FCSTD DOCUMENT  (FreeCAD 1.0R39109 (Git))
Label: main
License: All rights reserved
LicenseURL: https://en.wikipedia.org/wiki/All_rights_reserved
objects: Sketcher::SketchObject×1, PartDesign::Body×1
note: 3 computed .brp shape members not serialized (recipe doc carries the construction recipe); baked Part::Feature solids carry a one-line shape summary decoded from their .brp

FEATURE [Sketcher::SketchObject] Sketch
  ArcFitTolerance = 1e-06
  AttachmentSupport = -> [XY_Plane]
  FullyConstrained = true
  MakeInternals = false
  MapMode = 5
  sketch-geometry (28):
    g0: Circle CenterX=-90 CenterY=0 CenterZ=0 NormalX=0 NormalY=0 NormalZ=1 AngleXU=0 Radius=57
    g1: Circle CenterX=0 CenterY=90 CenterZ=0 NormalX=0 NormalY=0 NormalZ=1 AngleXU=0 Radius=57
    g2: Circle CenterX=90 CenterY=0 CenterZ=0 NormalX=0 NormalY=0 NormalZ=1 AngleXU=0 Radius=57
    g3: Circle CenterX=0 CenterY=-90 CenterZ=0 NormalX=0 NormalY=0 NormalZ=1 AngleXU=0 Radius=57
    g4: Circle [constr] CenterX=0 CenterY=0 CenterZ=0 NormalX=0 NormalY=0 NormalZ=1 AngleXU=0 Radius=90
    g5: Circle CenterX=0 CenterY=0 CenterZ=0 NormalX=0 NormalY=0 NormalZ=1 AngleXU=0 Radius=14
    g6: ArcOfCircle CenterX=0 CenterY=90 CenterZ=0 NormalX=0 NormalY=0 NormalZ=1 AngleXU=0 Radius=75 StartAngle=0.0646876 EndAngle=3.07691
    g7: ArcOfCircle CenterX=90 CenterY=0 CenterZ=0 NormalX=0 NormalY=0 NormalZ=1 AngleXU=0 Radius=75 StartAngle=4.77708 EndAngle=7.78929
    g8: ArcOfCircle CenterX=0 CenterY=-90 CenterZ=0 NormalX=0 NormalY=0 NormalZ=1 AngleXU=0 Radius=75 StartAngle=3.20628 EndAngle=6.2185
    g9: ArcOfCircle CenterX=-90 CenterY=0 CenterZ=0 NormalX=0 NormalY=0 NormalZ=1 AngleXU=0 Radius=75 StartAngle=1.63548 EndAngle=4.6477
    g10: ArcOfCircle CenterX=-81.3173 CenterY=81.3173 CenterZ=0 NormalX=0 NormalY=0 NormalZ=1 AngleXU=0 Radius=15 StartAngle=1.12452 EndAngle=3.58787
    g11: LineSegment [constr] StartX=-81.3173 StartY=81.3173 StartZ=0 EndX=0 EndY=0 EndZ=0
    g12: ArcOfCircle CenterX=81.3173 CenterY=81.3173 CenterZ=0 NormalX=0 NormalY=0 NormalZ=1 AngleXU=0 Radius=15 StartAngle=5.83691 EndAngle=8.30026
    g13: ArcOfCircle CenterX=81.3173 CenterY=-81.3173 CenterZ=0 NormalX=0 NormalY=0 NormalZ=1 AngleXU=0 Radius=15 StartAngle=4.26611 EndAngle=6.72946
    g14: ArcOfCircle CenterX=-81.3173 CenterY=-81.3173 CenterZ=0 NormalX=0 NormalY=0 NormalZ=1 AngleXU=0 Radius=15 StartAngle=2.69532 EndAngle=5.15867
    g15: LineSegment [constr] StartX=0 StartY=0 StartZ=0 EndX=81.3173 EndY=81.3173 EndZ=0
    g16: LineSegment [constr] StartX=0 StartY=0 StartZ=0 EndX=81.3173 EndY=-81.3173 EndZ=0
    g17: LineSegment [constr] StartX=-81.3173 StartY=-81.3173 StartZ=0 EndX=0 EndY=0 EndZ=0
    g18: Circle [constr] CenterX=0 CenterY=0 CenterZ=0 NormalX=0 NormalY=0 NormalZ=1 AngleXU=0 Radius=115
    g19: Circle CenterX=-81.3173 CenterY=81.3173 CenterZ=0 NormalX=0 NormalY=0 NormalZ=1 AngleXU=0 Radius=4.75
    g20: Circle CenterX=81.3173 CenterY=81.3173 CenterZ=0 NormalX=0 NormalY=0 NormalZ=1 AngleXU=0 Radius=4.75
    g21: Circle CenterX=81.3173 CenterY=-81.3173 CenterZ=0 NormalX=0 NormalY=0 NormalZ=1 AngleXU=0 Radius=4.75
    g22: Circle CenterX=-81.3173 CenterY=-81.3173 CenterZ=0 NormalX=0 NormalY=0 NormalZ=1 AngleXU=0 Radius=4.75
    g23: Circle [constr] CenterX=0 CenterY=0 CenterZ=0 NormalX=0 NormalY=0 NormalZ=1 AngleXU=0 Radius=20
    g24: Circle CenterX=20 CenterY=0 CenterZ=0 NormalX=0 NormalY=0 NormalZ=1 AngleXU=0 Radius=1.5
    g25: Circle CenterX=0 CenterY=20 CenterZ=0 NormalX=0 NormalY=0 NormalZ=1 AngleXU=0 Radius=1.5
    g26: Circle CenterX=-20 CenterY=0 CenterZ=0 NormalX=0 NormalY=0 NormalZ=1 AngleXU=0 Radius=1.5
    g27: Circle CenterX=0 CenterY=-20 CenterZ=0 NormalX=0 NormalY=0 NormalZ=1 AngleXU=0 Radius=1.5
  constraints (76):
    c: PointOnObject(g0,g-1)
    c: PointOnObject(g1,g-2)
    c: PointOnObject(g2,g-1)
    c: PointOnObject(g3,g-2)
    c: Equal(g3,g2)
    c: Equal(g2,g1)
    c: Equal(g1,g0)
    c: PointOnObject(g3,g4)
    c: PointOnObject(g2,g4)
    c: PointOnObject(g1,g4)
    c: PointOnObject(g0,g4)
    c: Diameter(g2) = 114
    c: Diameter(g5) = 28
    c: Diameter(g4) = 180
    c: Coincident(g6,g1)
    c: Coincident(g7,g2)
    c: Coincident(g8,g3)
    c: Coincident(g9,g0)
    c: Equal(g9,g6)
    c: Equal(g6,g7)
    c: Equal(g8,g7)
    c: Coincident(g4,g5)
    c: Coincident(g4,g-1)
    c: Coincident(g6,g10)
    c: Coincident(g9,g10)
    c: Coincident(g11,g10)
    c: Coincident(g11,g4)
    c: Angle(g-2,g11) = 0.785398
    c: Coincident(g9,g14)
    c: Coincident(g8,g14)
    c: Coincident(g8,g13)
    c: Coincident(g7,g13)
    c: Coincident(g7,g12)
    c: Coincident(g6,g12)
    c: Coincident(g15,g4)
    c: Coincident(g15,g12)
    c: Coincident(g16,g4)
    c: Coincident(g16,g13)
    c: Coincident(g17,g14)
    c: Coincident(g17,g4)
    c: Angle(g15,g-2) = 0.785398
    c: Angle(g16,g-1) = 0.785398
    c: Angle(g17,g-2) = 0.785398
    c: Coincident(g18,g4)
    c: PointOnObject(g12,g18)
    c: PointOnObject(g10,g18)
    c: PointOnObject(g14,g18)
    c: PointOnObject(g13,g18)
    c: Diameter(g18) = 230
    c: Radius(g7) = 75
    c: Equal(g12,g10)
    c: Equal(g13,g14)
    c: Equal(g14,g10)
    c: Radius(g12) = 15
    c: Coincident(g19,g10)
    c: Diameter(g19) = 9.5
    c: Coincident(g20,g12)
    c: Coincident(g21,g13)
    c: Coincident(g22,g14)
    c: Equal(g22,g21)
    c: Equal(g21,g20)
    c: Equal(g20,g19)
    c: Coincident(g23,g4)
    c: PointOnObject(g24,g23)
    c: PointOnObject(g25,g23)
    c: PointOnObject(g26,g23)
    c: PointOnObject(g27,g23)
    c: Horizontal(g24,g4)
    c: Horizontal(g4,g26)
    c: Vertical(g4,g25)
    c: Vertical(g4,g27)
    c: Equal(g24,g25)
    c: Equal(g25,g26)
    c: Equal(g26,g27)
    c: Diameter(g25) = 3
    c: Diameter(g23) = 40
FEATURE [PartDesign::Body] Body
  AllowCompound = false
  Group = -> [Sketch]
  Origin = -> Origin
